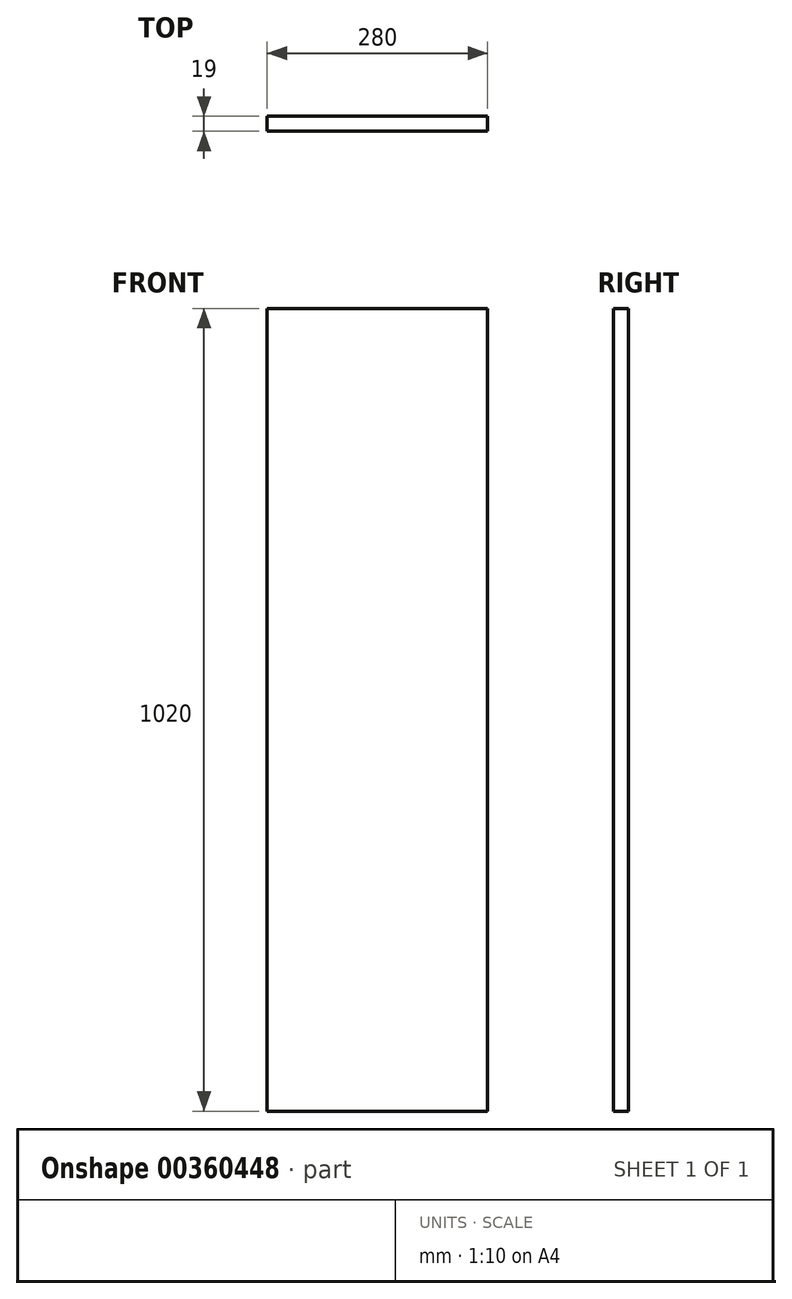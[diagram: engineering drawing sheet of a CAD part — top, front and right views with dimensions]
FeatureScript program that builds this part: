
annotation { "Feature Type Name" : "Feature", "Feature Type Description" : "" }
export const myFeature = defineFeature(function(context is Context, id is Id, definition is map)
    precondition{}
    {
        {
            var Q0;
            Q0=qCreatedBy(makeId("Front.planeOp"),FACE);
            var sketch = newSketch(context, id + "F0", { "sketchPlane" : qUnion([Q0])});
            skLineSegment(sketch, "E0.bottom", {"start": v(280, 1020) * mm, "end": v(0, 1020) * mm});
            skLineSegment(sketch, "E0.top", {"start": v(280, 0) * mm, "end": v(0, 0) * mm});
            skLineSegment(sketch, "E0.left", {"start": v(280, 1020) * mm, "end": v(280, 0) * mm});
            skLineSegment(sketch, "E0.right", {"start": v(0, 1020) * mm, "end": v(0, 0) * mm});
            skSolve(sketch);
        }
        {
            var Q0;
            Q0=makeQuery(id+"F0.imprint","IMPRINT",FACE,{"disambiguationData":[TD([[makeQuery(id+"F0.imprint","IMPRINT",EDGE,{"derivedFrom":sQuery(id+"F0.wireOp",EDGE,"E0.bottom")}),1.0]])]});
            extrude(context, id + "F1", {"entities" : qUnion([Q0]), "depth" : 19 * mm});
        }
    });
